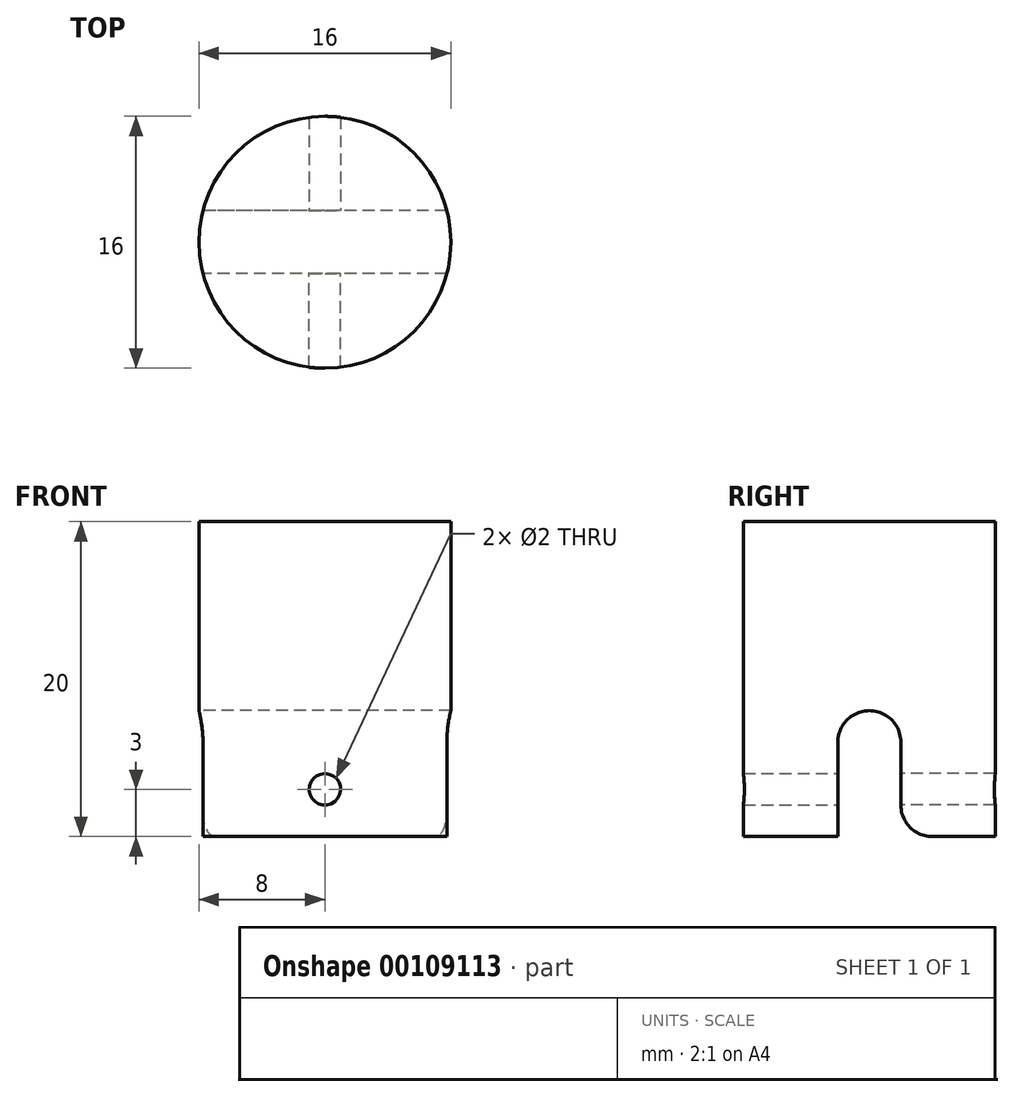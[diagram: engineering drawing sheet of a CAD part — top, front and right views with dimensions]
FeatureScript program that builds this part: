
annotation { "Feature Type Name" : "Feature", "Feature Type Description" : "" }
export const myFeature = defineFeature(function(context is Context, id is Id, definition is map)
    precondition{}
    {
        {
            var Q0;
            Q0=qCreatedBy(makeId("Top.planeOp"),FACE);
            var sketch = newSketch(context, id + "F0", { "sketchPlane" : qUnion([Q0])});
            skCircle(sketch, "E0", {"center": v(0, 0) * mm, "radius": 8 * mm});
            skSolve(sketch);
        }
        {
            var Q0;
            Q0=makeQuery(id+"F0.imprint","IMPRINT",FACE,{"disambiguationData":[TD([[makeQuery(id+"F0.imprint","IMPRINT",EDGE,{"derivedFrom":sQuery(id+"F0.wireOp",EDGE,"E0")}),1.0]])]});
            extrude(context, id + "F1", {"entities" : qUnion([Q0]), "depth" : 20 * mm});
        }
        {
            var Q0;
            Q0=makeQuery(id+"F0.imprint","IMPRINT",FACE,{"disambiguationData":[TD([[makeQuery(id+"F0.imprint","IMPRINT",EDGE,{"derivedFrom":sQuery(id+"F0.wireOp",EDGE,"E0")}),1.0]])]});
            var sketch = newSketch(context, id + "F2", { "sketchPlane" : qUnion([Q0])});
            skLineSegment(sketch, "E1.bottom", {"start": v(8, 2) * mm, "end": v(-8, 2) * mm});
            skLineSegment(sketch, "E1.top", {"start": v(8, -2) * mm, "end": v(-8, -2) * mm});
            skLineSegment(sketch, "E1.left", {"start": v(8, 2) * mm, "end": v(8, -2) * mm});
            skLineSegment(sketch, "E1.right", {"start": v(-8, 2) * mm, "end": v(-8, -2) * mm});
            skPoint(sketch, "E1.middle", {"position": v(0, 0) * mm});
            skSolve(sketch);
        }
        {
            var Q0;
            {var subQ0=sQuery(id+"F2.wireOp",EDGE,"E1.bottom");var subQ1=makeQuery(id+"F0.imprint","IMPRINT",EDGE,{"derivedFrom":sQuery(id+"F0.wireOp",EDGE,"E0")});var subQ4=makeQuery(id+"F2.imprint","INTERSECT",VERTEX,{"disambiguationData":[OD(0.0)],"derivedFrom":[subQ1,subQ0]});Q0=makeQuery(id+"F2.imprint","IMPRINT",FACE,{"disambiguationData":[TD([[makeQuery(id+"F2.imprint","IMPRINT",EDGE,{"disambiguationData":[TD([[subQ4,-1.0]])],"derivedFrom":subQ0}),1.0]])]});}
            extrude(context, id + "F3", {"entities" : qUnion([Q0]), "operationType" : NewBodyOperationType.REMOVE, "depth" : 8 * mm});
        }
        {
            var Q0;
            Q0=makeQuery(id+"F3.boolean.opBoolean","COPY",FACE,{"derivedFrom":makeQuery(id+"F3.opExtrude","SWEPT_FACE",FACE,{"disambiguationData":[OSD([sQuery(id+"F2.wireOp",EDGE,"E1.top")])]})});
            var sketch = newSketch(context, id + "F4", { "sketchPlane" : qUnion([Q0])});
            skCircle(sketch, "E2", {"center": v(0, 3) * mm, "radius": 1 * mm});
            skSolve(sketch);
        }
        {
            var Q0;
            Q0=sQuery(id+"F4.wireOp",VERTEX,"E2.center");
            var Q1;
            Q1=makeQuery(id+"F1.opExtrude","SWEPT_BODY",BODY,{"disambiguationData":[OSD([sQuery(id+"F0.wireOp",EDGE,"E0")])]});
            hole(context, id + "F5", {"style" : HoleStyle.SIMPLE, "endStyle" : HoleEndStyle.THROUGH, "holeDiameter" : 2 * mm, "locations" : qUnion([Q0]), "scope" : qUnion([Q1]), "isTappedThrough" : true});
        }
        {
            var Q0;
            Q0=makeQuery(id+"F3.boolean.opBoolean","COPY",FACE,{"derivedFrom":makeQuery(id+"F3.opExtrude","SWEPT_FACE",FACE,{"disambiguationData":[OSD([sQuery(id+"F2.wireOp",EDGE,"E1.bottom")])]})});
            var sketch = newSketch(context, id + "F6", { "sketchPlane" : qUnion([Q0])});
            skCircle(sketch, "E3", {"center": v(0, 3) * mm, "radius": 1 * mm});
            skSolve(sketch);
        }
        {
            var Q0;
            Q0=sQuery(id+"F6.wireOp",VERTEX,"E3.center");
            var Q1;
            Q1=makeQuery(id+"F1.opExtrude","SWEPT_BODY",BODY,{"disambiguationData":[OSD([sQuery(id+"F0.wireOp",EDGE,"E0")])]});
            hole(context, id + "F7", {"style" : HoleStyle.SIMPLE, "endStyle" : HoleEndStyle.THROUGH, "holeDiameter" : 2 * mm, "locations" : qUnion([Q0]), "scope" : qUnion([Q1]), "isTappedThrough" : true});
        }
        {
            var Q0;
            Q0=makeQuery(id+"F3.boolean.opBoolean","COPY",EDGE,{"derivedFrom":makeQuery(id+"F3.opExtrude","CAP_EDGE",EDGE,{"disambiguationData":[OSD([sQuery(id+"F2.wireOp",EDGE,"E1.bottom")])],"isStart":true})});
            var Q1;
            Q1=makeQuery(id+"F3.boolean.opBoolean","COPY",EDGE,{"derivedFrom":makeQuery(id+"F3.opExtrude","CAP_EDGE",EDGE,{"disambiguationData":[OSD([sQuery(id+"F2.wireOp",EDGE,"E1.top")])],"isStart":true})});
            fillet(context, id + "F8", {"entities" : qUnion([Q0, Q1]), "radius" : 2 * mm, "tangentPropagation" : true, "allowEdgeOverflow" : false});
        }
        {
            var Q0;
            Q0=makeQuery(id+"F3.boolean.opBoolean","COPY",EDGE,{"derivedFrom":makeQuery(id+"F3.opExtrude","CAP_EDGE",EDGE,{"disambiguationData":[OSD([sQuery(id+"F2.wireOp",EDGE,"E1.bottom")])],"isStart":false})});
            var Q1;
            Q1=makeQuery(id+"F3.boolean.opBoolean","COPY",EDGE,{"derivedFrom":makeQuery(id+"F3.opExtrude","CAP_EDGE",EDGE,{"disambiguationData":[OSD([sQuery(id+"F2.wireOp",EDGE,"E1.top")])],"isStart":false})});
            fillet(context, id + "F9", {"entities" : qUnion([Q0, Q1]), "radius" : 2 * mm, "tangentPropagation" : true, "allowEdgeOverflow" : false});
        }
    });
